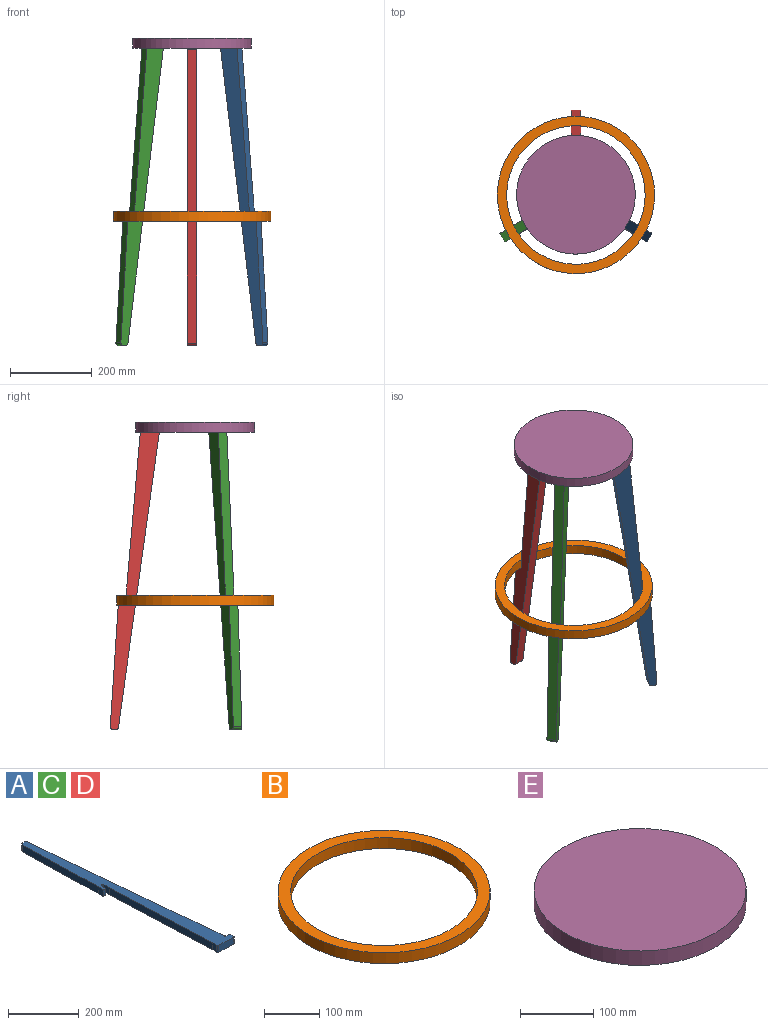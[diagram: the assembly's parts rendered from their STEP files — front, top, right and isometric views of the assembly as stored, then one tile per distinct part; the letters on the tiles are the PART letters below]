
ASSEMBLY  parts=5 mates=2
PART A: 21 faces, bbox 106.4x750.9x24 mm
  f0: plane 24x11.99mm, normal (1,-0.04,0), area 288mm2, adj f1,f18,f19,f20
  f1: cylinder r=4mm len=24mm, axis (0,0,-1), area 150.8mm2, adj f0,f2,f19,f20
  f2: plane 24x10.88mm, normal (0.04,1,0), area 261.3mm2, adj f1,f3,f19,f20
  f3: cylinder r=4mm len=24mm, axis (0,0,-1), area 137.6mm2, adj f2,f4,f19,f20
  f4: plane 720.18x67.82mm, normal (1,0.09,0), area 17360.9mm2, adj f3,f5,f19,f20
  f5: cylinder r=7mm len=24mm, axis (0,0,-1), area 240.7mm2, adj f4,f6,f19,f20
  f6: plane 24x6.09mm, normal (0.04,1,0), area 146.3mm2, adj f5,f7,f19,f20
  f7: cylinder r=7mm len=24mm, axis (0,0,-1), area 274.9mm2, adj f6,f8,f19,f20
  f8: plane 295.62x24mm, normal (-1,-0.02,0), area 7096.5mm2, adj f7,f9,f19,f20
  f9: plane 24x20.98mm, normal (-1,0.04,0), area 504mm2, adj f8,f10,f19,f20
  f10: plane 24x9.99mm, normal (-0.04,-1,0), area 240mm2, adj f9,f11,f19,f20
  f11: plane 24x16.98mm, normal (1,-0.04,0), area 408mm2, adj f10,f12,f19,f20
  f12: cylinder r=4.56mm len=24mm, axis (0,0,-1), area 343.8mm2, adj f11,f13,f19,f20
  f13: plane 24x21.98mm, normal (-1,0.04,0), area 528mm2, adj f12,f14,f19,f20
  f14: plane 398.63x24mm, normal (-1,-0.04,0), area 9576mm2, adj f13,f15,f19,f20
  f15: plane 24x15.98mm, normal (-1,0.04,0), area 384mm2, adj f14,f16,f19,f20
  f16: cylinder r=4mm len=24mm, axis (0,0,-1), area 150.8mm2, adj f15,f17,f19,f20
  f17: plane 56.95x24mm, normal (-0.04,-1,0), area 1368mm2, adj f16,f18,f19,f20
  f18: cylinder r=4mm len=24mm, axis (0,0,-1), area 150.8mm2, adj f0,f17,f19,f20
  f19: plane 750.88x106.39mm, normal (0,0,1), area 25896.7mm2, adj f0,f1,f2,f3,f4,f5,f6,f7
  f20: plane 750.88x106.39mm, normal (0,0,-1), area 25896.7mm2, adj f0,f1,f2,f3,f4,f5,f6,f7
PART B: 31 faces, bbox 384x384x24 mm
  f0: plane 20x12.69mm, normal (0,-1,0), area 253.7mm2, adj f1,f23,f27,f28
  f1: cylinder r=4mm len=20mm, axis (0,0,-1), area 252.9mm2, adj f0,f2,f27,f28
  f2: plane 20x4.34mm, normal (-1,0,0), area 86.9mm2, adj f1,f3,f27,f28
  f3: cylinder r=4mm len=20mm, axis (0,0,-1), area 251.3mm2, adj f2,f4,f27,f28
  f4: plane 20x8mm, normal (0,1,0), area 160mm2, adj f3,f5,f27,f28
  f5: cylinder r=4mm len=20mm, axis (0,0,-1), area 251.3mm2, adj f4,f6,f27,f28
  f6: plane 20x4.34mm, normal (1,0,0), area 86.9mm2, adj f5,f23,f27,f28
  f7: plane 20x10.99mm, normal (0.87,0.5,0), area 253.7mm2, adj f8,f21,f27,f30
  f8: cylinder r=4mm len=20mm, axis (0,0,-1), area 252.9mm2, adj f7,f9,f27,f30
  f9: plane 20x3.76mm, normal (0.5,-0.87,0), area 86.9mm2, adj f8,f10,f27,f30
  f10: cylinder r=4mm len=20mm, axis (0,0,-1), area 251.3mm2, adj f9,f11,f27,f30
  f11: plane 20x6.93mm, normal (-0.87,-0.5,0), area 160mm2, adj f10,f12,f27,f30
  f12: cylinder r=4mm len=20mm, axis (0,0,-1), area 251.3mm2, adj f11,f13,f27,f30
  f13: plane 20x3.76mm, normal (-0.5,0.87,0), area 86.9mm2, adj f12,f21,f27,f30
  f14: plane 20x10.99mm, normal (-0.87,0.5,0), area 253.7mm2, adj f15,f22,f27,f29
  f15: cylinder r=4mm len=20mm, axis (0,0,-1), area 252.9mm2, adj f14,f16,f27,f29
  f16: plane 20x3.76mm, normal (0.5,0.87,0), area 86.9mm2, adj f15,f17,f27,f29
  f17: cylinder r=4mm len=20mm, axis (0,0,-1), area 251.3mm2, adj f16,f18,f27,f29
  f18: plane 20x6.93mm, normal (0.87,-0.5,0), area 160mm2, adj f17,f19,f27,f29
  f19: cylinder r=4mm len=20mm, axis (0,0,-1), area 251.3mm2, adj f18,f20,f27,f29
  f20: plane 20x3.76mm, normal (-0.5,-0.87,0), area 86.9mm2, adj f19,f22,f27,f29
  f21: cylinder r=4mm len=20mm, axis (0,0,-1), area 252.9mm2, adj f7,f13,f27,f30
  f22: cylinder r=4mm len=20mm, axis (0,0,-1), area 252.9mm2, adj f14,f20,f27,f29
  f23: cylinder r=4mm len=20mm, axis (0,0,-1), area 252.9mm2, adj f0,f6,f27,f28
  f24: cylinder r=169mm len=338mm, axis (0,0,-1), area 25484.6mm2, adj f26,f27
  f25: cylinder r=192mm len=384mm, axis (0,0,-1), area 28952.9mm2, adj f26,f27
  f26: plane 384x384mm, normal (0,0,1), area 26084.6mm2, adj f24,f25
  f27: plane 384x384mm, normal (0,0,-1), area 25157.1mm2, adj f0,f1,f2,f3,f4,f5,f6,f7
  f28: plane 26.4x15.2mm, normal (0,0,-1), area 309.2mm2, adj f0,f1,f2,f3,f4,f5,f6,f23
  f29: plane 26.5x22.84mm, normal (0,0,-1), area 309.2mm2, adj f14,f15,f16,f17,f18,f19,f20,f22
  f30: plane 26.5x22.84mm, normal (0,0,-1), area 309.2mm2, adj f7,f8,f9,f10,f11,f12,f13,f21
PART C: same geometry as A
PART D: same geometry as A
PART E: 30 faces, bbox 290x290x24 mm
  f0: cylinder r=4mm len=20mm, axis (0,0,-1), area 252.9mm2, adj f1,f23,f26,f27
  f1: plane 20x12.69mm, normal (0,1,0), area 253.7mm2, adj f0,f2,f26,f27
  f2: cylinder r=4mm len=20mm, axis (0,0,-1), area 252.9mm2, adj f1,f3,f26,f27
  f3: plane 53.69x20mm, normal (1,0,0), area 1073.7mm2, adj f2,f4,f26,f27
  f4: cylinder r=4mm len=20mm, axis (0,0,-1), area 252.9mm2, adj f3,f5,f26,f27
  f5: plane 20x12.69mm, normal (0,-1,0), area 253.7mm2, adj f4,f6,f26,f27
  f6: cylinder r=4mm len=20mm, axis (0,0,-1), area 252.9mm2, adj f5,f23,f26,f27
  f7: cylinder r=4mm len=20mm, axis (0,0,-1), area 252.9mm2, adj f8,f21,f26,f29
  f8: plane 46.49x26.84mm, normal (0.5,-0.87,0), area 1073.7mm2, adj f7,f9,f26,f29
  f9: cylinder r=4mm len=20mm, axis (0,0,-1), area 252.9mm2, adj f8,f10,f26,f29
  f10: plane 20x10.99mm, normal (-0.87,-0.5,0), area 253.7mm2, adj f9,f11,f26,f29
  f11: cylinder r=4mm len=20mm, axis (0,0,-1), area 252.9mm2, adj f10,f12,f26,f29
  f12: plane 46.49x26.84mm, normal (-0.5,0.87,0), area 1073.7mm2, adj f11,f13,f26,f29
  f13: cylinder r=4mm len=20mm, axis (0,0,-1), area 252.9mm2, adj f12,f21,f26,f29
  f14: cylinder r=4mm len=20mm, axis (0,0,-1), area 252.9mm2, adj f15,f22,f26,f28
  f15: plane 46.49x26.84mm, normal (0.5,0.87,0), area 1073.7mm2, adj f14,f16,f26,f28
  f16: cylinder r=4mm len=20mm, axis (0,0,-1), area 252.9mm2, adj f15,f17,f26,f28
  f17: plane 20x10.99mm, normal (0.87,-0.5,0), area 253.7mm2, adj f16,f18,f26,f28
  f18: cylinder r=4mm len=20mm, axis (0,0,-1), area 252.9mm2, adj f17,f19,f26,f28
  f19: plane 46.49x26.84mm, normal (-0.5,-0.87,0), area 1073.7mm2, adj f18,f20,f26,f28
  f20: cylinder r=4mm len=20mm, axis (0,0,-1), area 252.9mm2, adj f19,f22,f26,f28
  f21: plane 20x10.99mm, normal (0.87,0.5,0), area 253.7mm2, adj f7,f13,f26,f29
  f22: plane 20x10.99mm, normal (-0.87,0.5,0), area 253.7mm2, adj f14,f20,f26,f28
  f23: plane 53.69x20mm, normal (-1,0,0), area 1073.7mm2, adj f0,f6,f26,f27
  f24: cylinder r=145mm len=290mm, axis (0,0,-1), area 21865.5mm2, adj f25,f26
  f25: plane 290x290mm, normal (0,0,1), area 66052mm2, adj f24
  f26: plane 290x290mm, normal (0,0,-1), area 61258.5mm2, adj f0,f1,f2,f3,f4,f5,f6,f7
  f27: plane 67.4x26.4mm, normal (0,0,-1), area 1597.8mm2, adj f0,f1,f2,f3,f4,f5,f6,f23
  f28: plane 68.64x53.64mm, normal (0,0,-1), area 1597.8mm2, adj f14,f15,f16,f17,f18,f19,f20,f22
  f29: plane 68.64x53.64mm, normal (0,0,-1), area 1597.8mm2, adj f7,f8,f9,f10,f11,f12,f13,f21
PLACE A rot(axis=(-0.2,-0.69,0.7),160.7deg) t=(-1211.97,713.59,-448.2)mm
PLACE B rot(axis=(0,0,1),119.7deg) t=(-253.82,1651.88,-422.26)mm
PLACE C rot(axis=(-0.94,-0.23,0.27),94.5deg) t=(1223.97,692.8,-448.2)mm
PLACE D rot(axis=(-0.57,0.59,-0.57),118.6deg) t=(-12,-1406.39,-448.2)mm
PLACE E t=(1561,-597,0)mm
MATE fastened D.f17 <-> E.f27  axis (0,0,1) through (0,101.5,20)mm
MATE cylindrical B.f24 <-> E.f24  axis (0,0,-1) through (0,0,-410.26)mm
